# Revit family: IS_Connect_T9835_BIM_BE
name_source: partatom
category: Plumbing Fixtures
revit_build: Autodesk Revit 2015 (Build: 20140606_1530(x64)
units: mm (PartAtom-declared; Revit-internal decimal feet)

## types (1)
- T9835EO - Connect Porte pivotante 900 mm verre transparent
    Accesoires = www.idealstandard.be
    Afwerking = Zilverkleurig aluminium
    Auteur = Ideal Standard Produktions-GmbH
    Barcode = 8014140381891
    Beschrijvingdouchekop = 0
    Beschrijvinggarantie = Fabrieksgarantie
    BimObjectNaam = ISI_IdealStandard_Douche_Connect_T9835EO
    Breedte = 0
    BrutoGewicht = 0
    Cost = 0 $
    Default Elevation = 0 mm  [stored 0 ft]
    Description = Connect Porte pivotante 900 mm verre transparent
    Diepte = 0 mm  [stored 0 ft]
    Dimensions = 900 x 50 x 1980 mm
    Douchebak = No
    DuurEenheid = jaar
    Eigenschappen = Connect glazen draaideur 900mm in 4 mm transparant veiligheidsglas
behandeld met Ideal Clean. Met aluminium muurprofiel zilverkleurig.
Met geïntegreerde handgrepen. Hoogte 1900 mm. De deur opent
enkel naar buiten. Omkeerbaar. Voor nis- of hoekopstelling. Voor
hoekopstelling dient u 2 panelen te bestellen.
    Garantieonderdelen = 2
    GrootteAfvoergat = 0
    Hauteur = 1980 mm
    IfcExportAs = IfcValveTypes
    IfcExportType = SHOWERS
    Installatieinstructies = www.idealstandard.be
    Kleur = Aluminium zilverkleurig
    Largeur = 50 mm
    Lengte = 0 mm  [stored 0 ft]
    Longueur = 900 mm
    Manufacturer = www.idealstandard.be
    Materiaal = Veiligheidsglas
    Merk = Ideal Standard
    Model = T9835EO
    Nettogewicht = 22
    Productinformatie = www.idealstandard.be
    Telefoonnummer = 0032 2 325 66 00
    Typeconnectie = Sanitair
    URL = www.idealstandard.be
    Uniclass2015Beschrijving = Douche
    Uniclass2015Version = Products v1.1
    Urlproducent = www.idealstandard.be
    Versie = 1
    Vervangingskosten = 0
    Verwachtelevensduur = 25 jaar
    Volumeunits = liter

note: [stored X ft] marks values corroborated as IEEE doubles in the binary element streams (Revit-internal decimal feet)

## geometry (parser evidence)
native form markers: Blend x6, Sweep x1
no freeform markers — native parametric forms only
